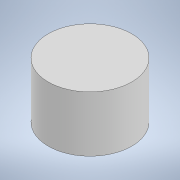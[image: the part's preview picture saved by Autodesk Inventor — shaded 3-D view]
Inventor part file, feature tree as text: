
AUTODESK INVENTOR PART (.ipt)
format: ipt  version: 2022.2 (Build 262287010, 287A)  size: 87,040 bytes
history: native  units: mm
features: extrude x1, sketch x1
ambient origin geometry x8: Origin, YZ Plane, XZ Plane, XY Plane, X Axis, Y Axis, Z Axis, Center Point
bodies: Solid1 (feature_tree)
feature tree (2):
  extrude  "Extrusion1"  Depth=8.0mm TaperAngle=0.0deg
  sketch  "Sketch1"  dims[d0=12.0mm d1=8.0mm d2=0.0mm]
